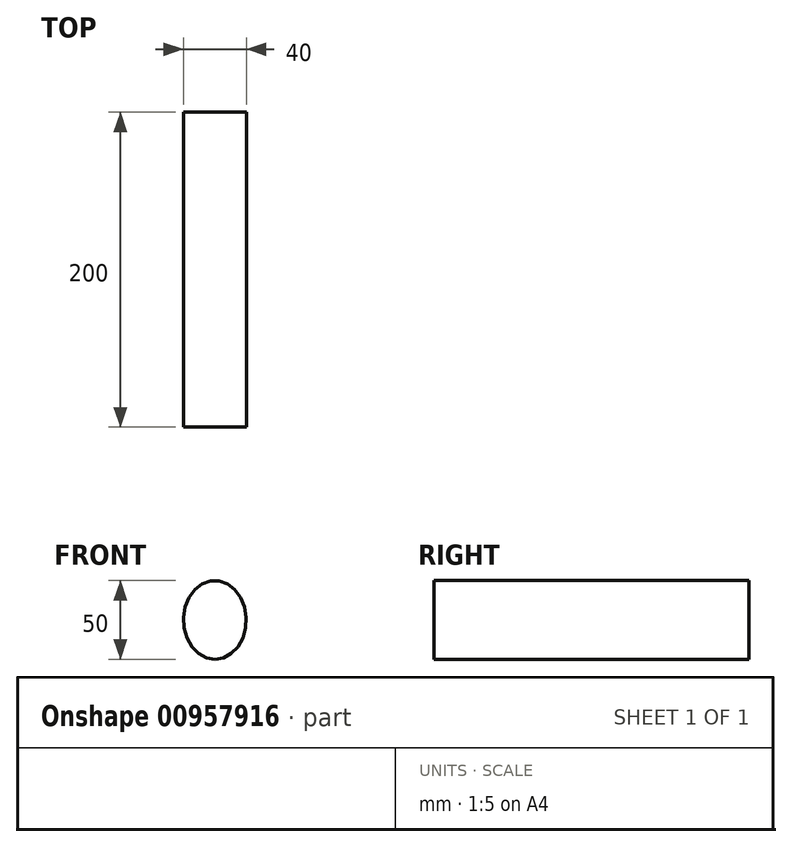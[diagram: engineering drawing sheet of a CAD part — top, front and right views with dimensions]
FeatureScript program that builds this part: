
annotation { "Feature Type Name" : "Feature", "Feature Type Description" : "" }
export const myFeature = defineFeature(function(context is Context, id is Id, definition is map)
    precondition{}
    {
        {
            var Q0;
            Q0=qCreatedBy(makeId("Front.planeOp"),FACE);
            var sketch = newSketch(context, id + "F0", { "sketchPlane" : qUnion([Q0])});
            skEllipse(sketch, "E0", {"center": v(0, 0) * mm, "majorRadius": 25 * mm, "minorRadius": 20 * mm, "majorAxis": v(0, -1)});
            skSolve(sketch);
        }
        {
            var Q0;
            Q0 = qSketchRegion(id + "F0", true);
            extrude(context, id + "F1", {"entities" : qUnion([Q0]), "oppositeDirection" : true, "depth" : 200 * mm, "offsetDistance" : 25.4 * mm});
        }
    });
